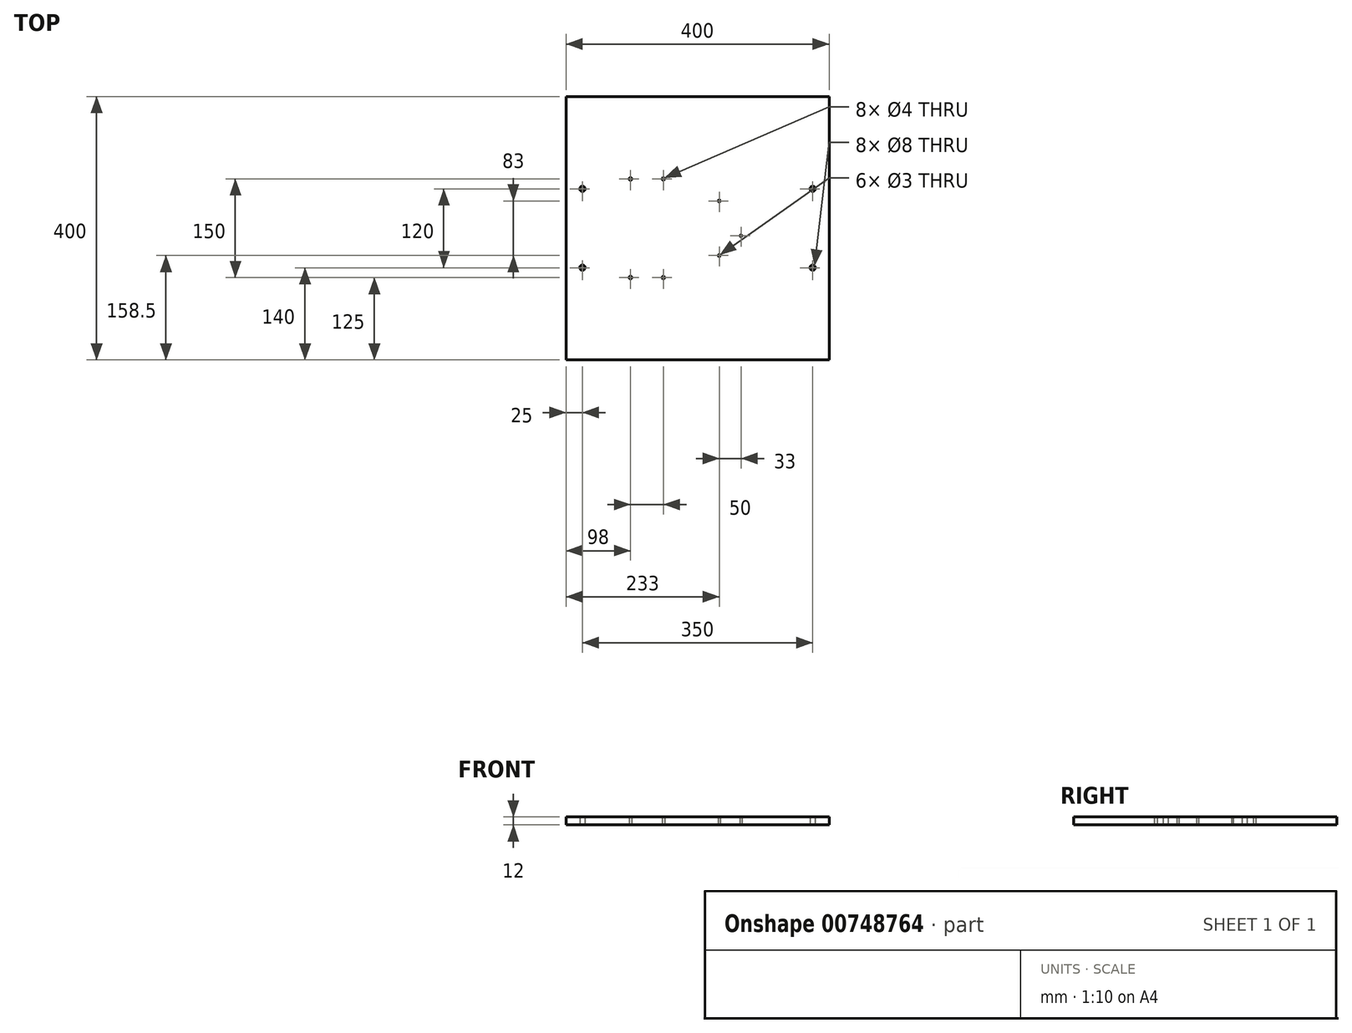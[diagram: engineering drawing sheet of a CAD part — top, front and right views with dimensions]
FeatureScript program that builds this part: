
annotation { "Feature Type Name" : "Feature", "Feature Type Description" : "" }
export const myFeature = defineFeature(function(context is Context, id is Id, definition is map)
    precondition{}
    {
        {
            var Q0;
            Q0=qCreatedBy(makeId("Top.planeOp"),FACE);
            var sketch = newSketch(context, id + "F0", { "sketchPlane" : qUnion([Q0])});
            skLineSegment(sketch, "E0.bottom", {"start": v(200, 200) * mm, "end": v(-200, 200) * mm});
            skLineSegment(sketch, "E0.top", {"start": v(200, -200) * mm, "end": v(-200, -200) * mm});
            skLineSegment(sketch, "E0.left", {"start": v(200, 200) * mm, "end": v(200, -200) * mm});
            skLineSegment(sketch, "E0.right", {"start": v(-200, 200) * mm, "end": v(-200, -200) * mm});
            skPoint(sketch, "E0.middle", {"position": v(0, 0) * mm});
            skCircle(sketch, "E1", {"center": v(-175, 60) * mm, "radius": 4 * mm});
            skCircle(sketch, "E2", {"center": v(-175, -60) * mm, "radius": 4 * mm});
            skCircle(sketch, "E3", {"center": v(175, 60) * mm, "radius": 4 * mm});
            skCircle(sketch, "E4", {"center": v(175, -60) * mm, "radius": 4 * mm});
            skLineSegment(sketch, "E5.bottom", {"start": v(-102, 75) * mm, "end": v(-52, 75) * mm, "construction": true});
            skLineSegment(sketch, "E5.top", {"start": v(-102, -75) * mm, "end": v(-52, -75) * mm, "construction": true});
            skLineSegment(sketch, "E5.left", {"start": v(-102, 75) * mm, "end": v(-102, -75) * mm, "construction": true});
            skLineSegment(sketch, "E5.right", {"start": v(-52, 75) * mm, "end": v(-52, -75) * mm, "construction": true});
            skCircle(sketch, "E6", {"center": v(-52, 75) * mm, "radius": 2 * mm});
            skCircle(sketch, "E7", {"center": v(-102, 75) * mm, "radius": 2 * mm});
            skCircle(sketch, "E8", {"center": v(-102, -75) * mm, "radius": 2 * mm});
            skCircle(sketch, "E9", {"center": v(-52, -75) * mm, "radius": 2 * mm});
            skLineSegment(sketch, "E10.bottom", {"start": v(66, 41.5) * mm, "end": v(33, 41.5) * mm, "construction": true});
            skLineSegment(sketch, "E10.top", {"start": v(66, -41.5) * mm, "end": v(33, -41.5) * mm, "construction": true});
            skLineSegment(sketch, "E10.left", {"start": v(66, 41.5) * mm, "end": v(66, -41.5) * mm, "construction": true});
            skLineSegment(sketch, "E10.right", {"start": v(33, 41.5) * mm, "end": v(33, -41.5) * mm, "construction": true});
            skCircle(sketch, "E11", {"center": v(33, 41.5) * mm, "radius": 1.5 * mm});
            skCircle(sketch, "E12", {"center": v(33, -41.5) * mm, "radius": 1.5 * mm});
            skCircle(sketch, "E13", {"center": v(66, -11.5) * mm, "radius": 1.5 * mm});
            skSolve(sketch);
        }
        {
            var Q0;
            Q0 = qSketchRegion(id + "F0", true);
            extrude(context, id + "F1", {"entities" : qUnion([Q0]), "depth" : 12 * mm, "offsetDistance" : 25 * mm});
        }
    });
